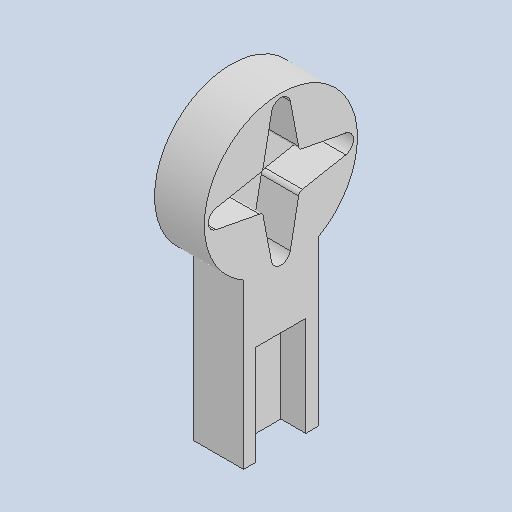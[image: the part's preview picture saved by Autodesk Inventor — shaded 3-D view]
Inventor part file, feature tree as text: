
AUTODESK INVENTOR PART (.ipt)
format: ipt  version: 2023 (Build 270158000, 158)  size: 132,608 bytes
history: native  units: in
note: dims shown in document units (in); Inventor stores cm internally (conversion verified against a paired STEP export)
features: other x3, sketch x3
ambient origin geometry x8: Origin, YZ Plane, XZ Plane, XY Plane, X Axis, Y Axis, Z Axis, Center Point
bodies: Solid1 (feature_tree)
feature tree (6):
  other  "Part_3_hand.ipt"
  other  "Solid1::Part_3_hand.ipt"
  other  "TaggingFeature1"
  sketch  "Sketch1"  dims[d0=0.3937in]
  sketch  "Sketch3"
  sketch  "Sketch4"
